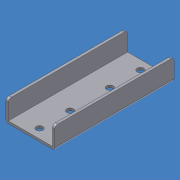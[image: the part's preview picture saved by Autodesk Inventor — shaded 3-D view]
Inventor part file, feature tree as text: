
AUTODESK INVENTOR PART (.ipt)
format: ipt  version: 2015 SP1 (Build 190203100, 203)  size: 180,736 bytes
history: native  units: mm
features: other x6, sheet_metal_op x5, sketch x4, plane x2, mirror x1, chamfer x1
ambient origin geometry x8: Origin, YZ Plane, XZ Plane, XY Plane, X Axis, Y Axis, Z Axis, Center Point
bodies: Solid1 (feature_tree)
feature tree (19):
  sheet_metal_op  "Face1"
  sheet_metal_op  "Flange1"
  sheet_metal_op  "Flange2"
  plane  "Work Plane1"
  mirror  "Mirror1"
  chamfer  "Corner Round1"
  plane  "Work Plane2"
  sketch  "Sketch1"  dims[d2=72.0mm]
  other  "Plate1"
  sketch  "Sketch2"  dims[d3=195.0mm]
  other  "Plate2"
  sheet_metal_op  "Bend1"
  sketch  "Sketch3"  dims[d4=0.001mm]
  other  "Plate3"
  sheet_metal_op  "Bend2"
  sketch  "Sketch4"  dims[d5=4.0mm d6=0.001mm d7=8.0mm d8=0.001mm d9=31.0mm d10=90.0deg d11=0.001mm d12=4.0mm d13=0.001mm d14=8.0mm d15=0.001mm d16=31.0mm d17=90.0deg d18=0.001mm d19=11.0mm d20=11.0mm d21=15.0mm d22=50.0mm d23=4.0mm d24=0.0mm d25=5.0mm d0=4.0mm]
  other  "FlatPattern"
  other  "Cut1"
  other  "FlatPatternExtrusion2"
